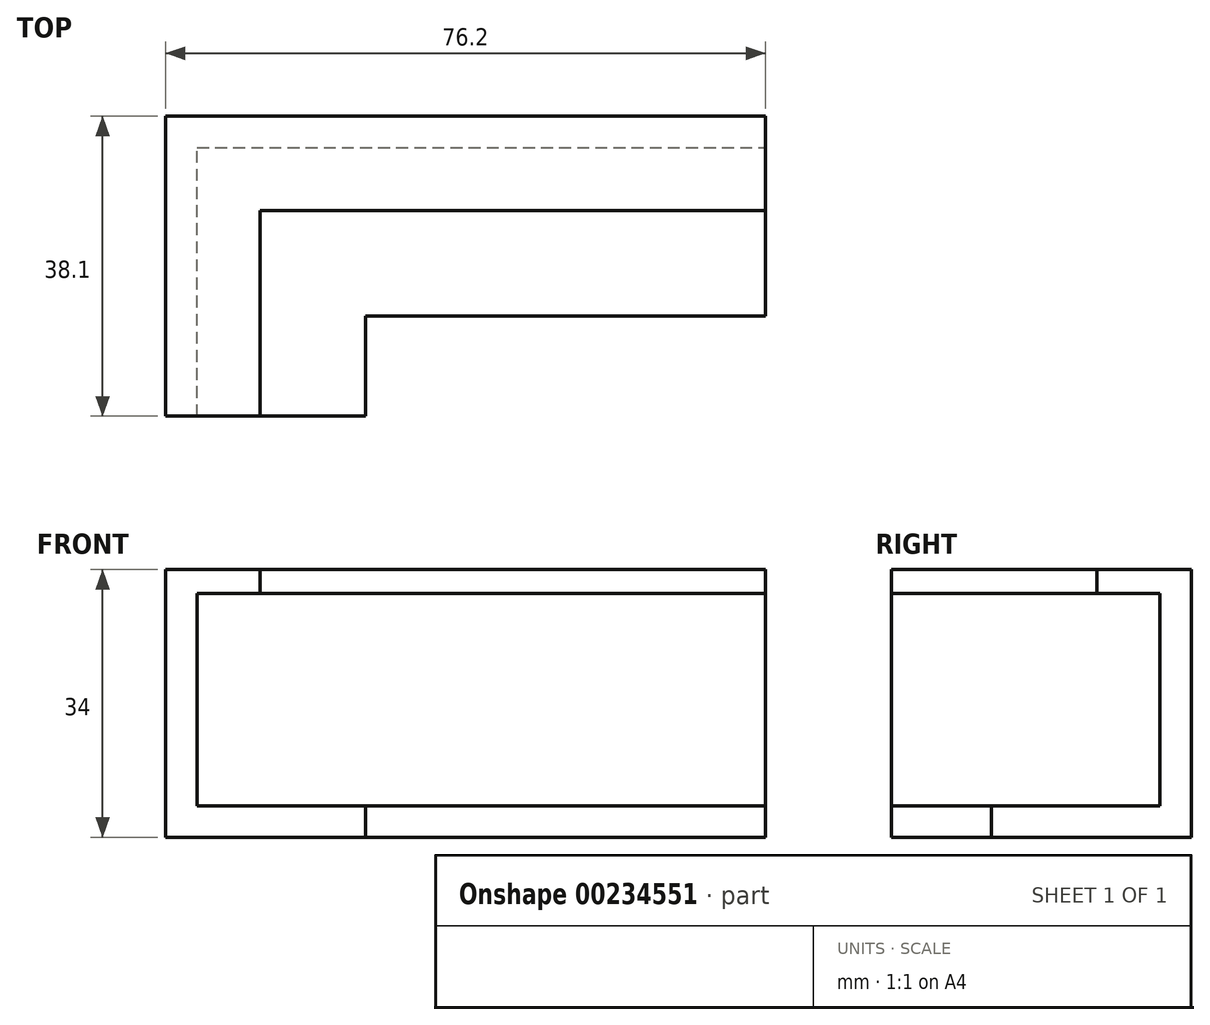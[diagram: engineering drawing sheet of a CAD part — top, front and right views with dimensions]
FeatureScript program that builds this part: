
annotation { "Feature Type Name" : "Feature", "Feature Type Description" : "" }
export const myFeature = defineFeature(function(context is Context, id is Id, definition is map)
    precondition{}
    {
        {
            var Q0;
            Q0=qCreatedBy(makeId("Top.planeOp"),FACE);
            var sketch = newSketch(context, id + "F0", { "sketchPlane" : qUnion([Q0])});
            skLineSegment(sketch, "E0", {"start": v(0, 0) * mm, "end": v(0, 38.1) * mm});
            skLineSegment(sketch, "E1", {"start": v(0, 38.1) * mm, "end": v(76.2, 38.1) * mm});
            skLineSegment(sketch, "E2", {"start": v(76.2, 38.1) * mm, "end": v(76.2, 12.7) * mm});
            skLineSegment(sketch, "E3", {"start": v(76.2, 12.7) * mm, "end": v(25.4, 12.7) * mm});
            skLineSegment(sketch, "E4", {"start": v(25.4, 12.7) * mm, "end": v(25.4, 0) * mm});
            skLineSegment(sketch, "E5", {"start": v(25.4, 0) * mm, "end": v(0, 0) * mm});
            skSolve(sketch);
        }
        {
            var Q0;
            Q0=makeQuery(id+"F0.imprint","IMPRINT",FACE,{"disambiguationData":[TD([[makeQuery(id+"F0.imprint","IMPRINT",EDGE,{"derivedFrom":sQuery(id+"F0.wireOp",EDGE,"E0")}),-1.0]])]});
            extrude(context, id + "F1", {"entities" : qUnion([Q0]), "depth" : 4 * mm});
        }
        {
            var Q0;
            Q0=makeQuery(id+"F1.opExtrude","CAP_FACE",FACE,{"disambiguationData":[OSD([sQuery(id+"F0.wireOp",EDGE,"E0"),sQuery(id+"F0.wireOp",EDGE,"E1"),sQuery(id+"F0.wireOp",EDGE,"E2"),sQuery(id+"F0.wireOp",EDGE,"E3"),sQuery(id+"F0.wireOp",EDGE,"E4"),sQuery(id+"F0.wireOp",EDGE,"E5")])],"isStart":false});
            var sketch = newSketch(context, id + "F2", { "sketchPlane" : qUnion([Q0])});
            skLineSegment(sketch, "E6", {"start": v(76.2, 38.1) * mm, "end": v(0, 38.1) * mm});
            skLineSegment(sketch, "E7", {"start": v(0, 38.1) * mm, "end": v(0, 0) * mm});
            skLineSegment(sketch, "E8", {"start": v(0, 0) * mm, "end": v(4, 0) * mm});
            skLineSegment(sketch, "E9", {"start": v(4, 0) * mm, "end": v(4, 34.1) * mm});
            skLineSegment(sketch, "E10", {"start": v(4, 34.1) * mm, "end": v(76.2, 34.1) * mm});
            skLineSegment(sketch, "E11", {"start": v(76.2, 34.1) * mm, "end": v(76.2, 38.1) * mm});
            skSolve(sketch);
        }
        {
            var Q0;
            Q0=makeQuery(id+"F2.imprint","IMPRINT",FACE,{"disambiguationData":[TD([[makeQuery(id+"F2.imprint","IMPRINT",EDGE,{"derivedFrom":sQuery(id+"F2.wireOp",EDGE,"E6")}),-1.0]])]});
            extrude(context, id + "F3", {"entities" : qUnion([Q0]), "operationType" : NewBodyOperationType.ADD, "depth" : 27 * mm});
        }
        {
            var Q0;
            Q0=makeQuery(id+"F3.opExtrude","CAP_FACE",FACE,{"disambiguationData":[OSD([sQuery(id+"F2.wireOp",EDGE,"E6"),sQuery(id+"F2.wireOp",EDGE,"E7"),sQuery(id+"F2.wireOp",EDGE,"E8"),sQuery(id+"F2.wireOp",EDGE,"E9"),sQuery(id+"F2.wireOp",EDGE,"E10"),sQuery(id+"F2.wireOp",EDGE,"E11")])],"isStart":false});
            var sketch = newSketch(context, id + "F4", { "sketchPlane" : qUnion([Q0])});
            skLineSegment(sketch, "E12", {"start": v(76.2, 38.1) * mm, "end": v(76.2, 26.1) * mm});
            skLineSegment(sketch, "E13", {"start": v(76.2, 26.1) * mm, "end": v(12, 26.1) * mm});
            skLineSegment(sketch, "E14", {"start": v(12, 26.1) * mm, "end": v(12, 0) * mm});
            skLineSegment(sketch, "E15", {"start": v(12, 0) * mm, "end": v(0, 0) * mm});
            skLineSegment(sketch, "E16", {"start": v(0, 0) * mm, "end": v(0, 38.1) * mm});
            skLineSegment(sketch, "E17", {"start": v(0, 38.1) * mm, "end": v(76.2, 38.1) * mm});
            skSolve(sketch);
        }
        {
            var Q0;
            {var subQ5=sQuery(id+"F4.wireOp",EDGE,"E13");Q0=makeQuery(id+"F4.imprint","IMPRINT",FACE,{"disambiguationData":[TD([[makeQuery(id+"F4.imprint","IMPRINT",EDGE,{"derivedFrom":subQ5}),-1.0]])]});}
            var Q1;
            {var subQ1=sQuery(id+"F4.wireOp",EDGE,"E16");Q1=makeQuery(id+"F4.imprint","IMPRINT",FACE,{"disambiguationData":[TD([[makeQuery(id+"F4.imprint","IMPRINT",EDGE,{"derivedFrom":subQ1}),-1.0]])]});}
            extrude(context, id + "F5", {"entities" : qUnion([Q0, Q1]), "operationType" : NewBodyOperationType.ADD, "depth" : 3 * mm});
        }
    });
